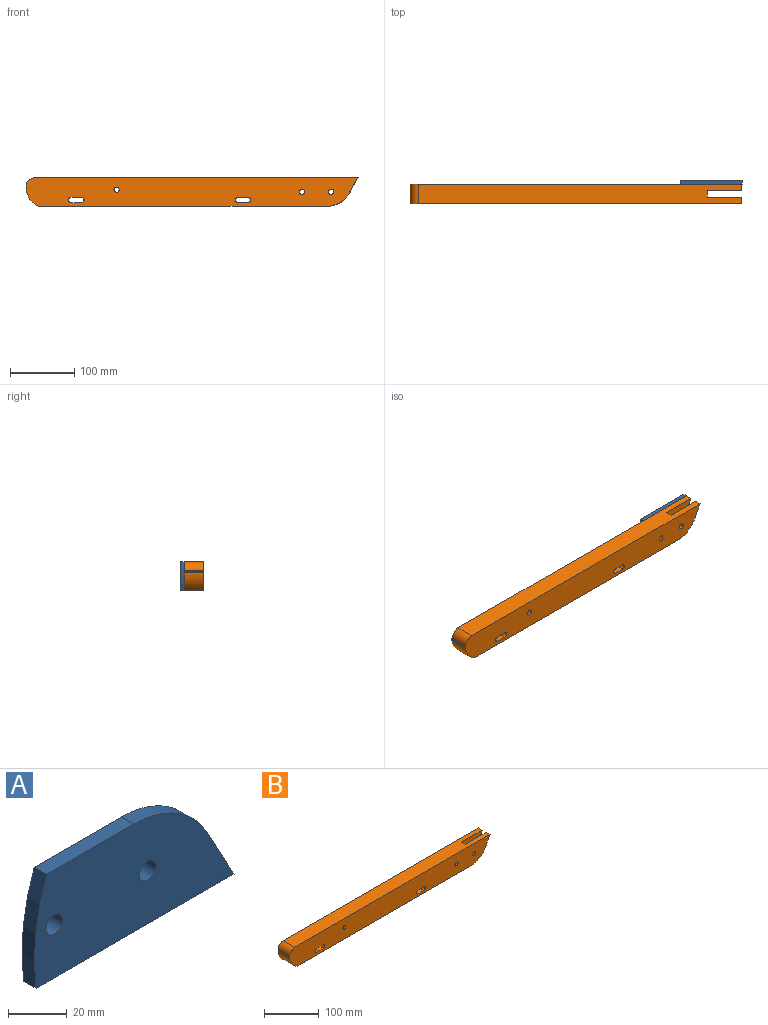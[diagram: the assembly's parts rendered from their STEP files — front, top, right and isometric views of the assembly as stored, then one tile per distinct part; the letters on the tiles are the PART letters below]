
ASSEMBLY  parts=2 mates=1
PART A: 9 faces, bbox 96.3x6x45 mm
  f0: plane 42.07x6mm, normal (0,0,1), area 252.4mm2, adj f1,f6,f7,f8
  f1: cylinder r=95mm len=45mm, axis (0,1,0), area 274.4mm2, adj f0,f2,f7,f8
  f2: plane 95.5x6mm, normal (0,0,-1), area 573mm2, adj f1,f3,f7,f8
  f3: plane 24.21x13.26mm, normal (0.88,0,0.48), area 165.6mm2, adj f2,f6,f7,f8
  f4: cylinder r=4mm len=8mm, axis (0,1,0), area 150.8mm2, adj f7,f8
  f5: cylinder r=4mm len=8mm, axis (0,1,0), area 150.8mm2, adj f7,f8
  f6: cylinder r=40mm len=35.08mm, axis (0,1,0), area 256.7mm2, adj f0,f3,f7,f8
  f7: plane 96.28x45mm, normal (0,-1,0), area 3518.7mm2, adj f0,f1,f2,f3,f4,f5,f6
  f8: plane 96.28x45mm, normal (0,1,0), area 3518.7mm2, adj f0,f1,f2,f3,f4,f5,f6
PART B: 28 faces, bbox 515.1x30x45 mm
  f0: plane 448.75x30mm, normal (0,0,-1), area 13128.5mm2, adj f1,f13,f14,f23,f24,f25,f26,f27
  f1: cylinder r=42.57mm len=35.19mm, axis (0,1,0), area 436.5mm2, adj f0,f2,f23,f26
  f2: plane 22.5x11.98mm, normal (0.88,0,-0.47), area 254.9mm2, adj f1,f3,f23,f26
  f3: plane 502.13x30mm, normal (0,0,1), area 14526.6mm2, adj f2,f15,f16,f23,f24,f25,f26,f27
  f4: cylinder r=4.31mm len=10mm, axis (0,1,0), area 270.7mm2, adj f23,f26
  f5: cylinder r=4mm len=30mm, axis (0,1,0), area 377mm2, adj f6,f22,f23,f24
  f6: plane 30x15mm, normal (0,0,-1), area 450mm2, adj f5,f7,f23,f24
  f7: cylinder r=4mm len=30mm, axis (0,1,0), area 377mm2, adj f6,f22,f23,f24
  f8: cylinder r=4mm len=30mm, axis (0,1,0), area 382.2mm2, adj f9,f17,f23,f24
  f9: plane 30x16.15mm, normal (0,0,-1), area 484.6mm2, adj f8,f10,f23,f24
  f10: cylinder r=4mm len=30mm, axis (0,1,0), area 382.2mm2, adj f9,f17,f23,f24
  f11: plane 30x1.42mm, normal (-1,0,0), area 42.6mm2, adj f12,f18,f23,f24
  f12: cylinder r=14.84mm len=30mm, axis (0,1,0), area 36.4mm2, adj f11,f13,f23,f24
  f13: cylinder r=34.88mm len=30mm, axis (0,1,0), area 1048.6mm2, adj f0,f12,f23,f24
  f14: cylinder r=42.57mm len=35.19mm, axis (0,1,0), area 436.5mm2, adj f0,f15,f24,f27
  f15: plane 22.5x11.98mm, normal (0.88,0,-0.47), area 254.9mm2, adj f3,f14,f24,f27
  f16: cylinder r=14.84mm len=30mm, axis (0,1,0), area 603.7mm2, adj f3,f18,f23,f24
  f17: plane 30x16.5mm, normal (0,0,1), area 495mm2, adj f8,f10,f23,f24
  f18: cylinder r=34.88mm len=30mm, axis (0,1,0), area 43.5mm2, adj f11,f16,f23,f24
  f19: cylinder r=4mm len=30mm, axis (0,1,0), area 754mm2, adj f23,f24
  f20: cylinder r=4mm len=30mm, axis (0,1,0), area 754mm2, adj f23,f24
  f21: cylinder r=4.31mm len=10mm, axis (0,1,0), area 270.7mm2, adj f24,f27
  f22: plane 30x15mm, normal (0,0,1), area 450mm2, adj f5,f7,f23,f24
  f23: plane 515.12x45mm, normal (0,-1,0), area 21807.9mm2, adj f0,f1,f2,f3,f4,f5,f6,f7
  f24: plane 515.12x45mm, normal (0,1,0), area 21807.9mm2, adj f0,f3,f5,f6,f7,f8,f9,f10
  f25: plane 45x26.81mm, normal (0.86,0,-0.51), area 523.8mm2, adj f0,f3,f26,f27
  f26: plane 80.55x45mm, normal (0,1,0), area 2317.9mm2, adj f0,f1,f2,f3,f4,f25
  f27: plane 80.55x45mm, normal (0,-1,0), area 2317.9mm2, adj f0,f3,f14,f15,f21,f25
PLACE A rot(axis=(-1,0,0),180deg) t=(172.76,78.77,3.67)mm
PLACE B t=(-130.01,78.77,-6.66)mm
MATE fastened B.f4 <-> A.f5  axis (0,1,0) through (79.99,78.77,-6.46)mm
